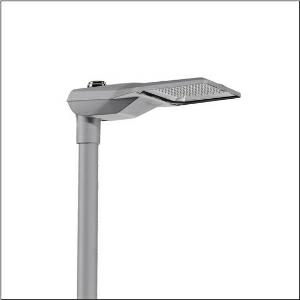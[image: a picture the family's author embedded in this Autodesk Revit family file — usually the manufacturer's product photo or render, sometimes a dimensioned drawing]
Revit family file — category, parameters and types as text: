
# Revit family: streetlight_sl_21_midi___st1_5a_5xe7p37n08mb_d4f4
name_source: partatom
category: Lighting Fixtures
units: mm (PartAtom-declared; Revit-internal decimal feet)

## family parameters
Cut with Voids When Loaded = No
Host = Face
Light Source = No
Part Type = Normal
Room Calculation Point = No
Round Connector Dimension = Use Diameter
Shared = No

## types (1)
- --- (1 x LED, 17960 lm, 136 W, 3000K)
    Apparent Load = 136 VA
    CIE Flux Codes = 22 53 95 100 100
    Color Rendering = 70
    Color Temperature = 3000K
    Default Elevation = 1800 mm
    Description = Streetlight SL 21 midi, mast luminaire, primary light control with lens, of PMMA, primary optical cover: cover, of toughened safety glass, transparent, light distribution: ST1.5a, light emission: direct distribution, primary light characteristic: asymmetric, installation type: side-entry, LED, 3G 2.5mm², High Power LED, rated luminous flux: 17.960lm, luminous efficacy: 132lm/W, light colour: 730, colour temperature: 3000K, control gear: NEMA (7pin), control: overheat protection, pre-setting: linear dimming characteristic, constant luminous flux control, time-dependent luminous flux control, flexible luminous flux parameterisation, mains connection: 220..240V, AC, 50/60Hz, connection cable pre-assembled, cable length: 12,5m, wiring characteristics: H05VV-F, start of lifetime: 136W, end of service life: 142W, reduction: 61W, luminaire housing, of diecast aluminium (EN AC-44300), powder-coated, SITECO metallic grey (DB 702S), corrosivity category C5 high according to DIN EN ISO 12944, multi-level sealing system, sealing non-destructively replaceable, inclination adjustable: 0°, 5°, 10°, 15°, length: 644mm, width: 335mm, height: 110mm, spigot size: 42mm (side-entry), mounting height: 4..8m, protection rating (complete): IP66, insulation class (complete): insulation class I (protective earthing), certification: CE, ENEC, ENEC+, VDE, impact resistance: IK10, permissible operating ambient temperature for outdoor applications: -40..+50°C, standard-compliant lighting for roads and squares, packaging unit: 1 piece

Light Distribution: ST1.5a
    Height = 111 mm
    Lamp = 1 x LED
    Lamp Light Flux = 17960 lm
    Lamp Power = 136 W
    Lamp count = 1
    Length = 644 mm
    Luminous efficacy = 132 lm/W
    Manufacturer = Siteco
    ModVariant = No
    Model = 5XE7P37N08MB
    Number of Poles = 1
    OnlyDefault = Yes
    Power Factor = 1
    Product Name = Streetlight SL 21 midi | ST1.5a
    Product group = mast luminaire | pylon top
    ProductGroupID = 6100
    Protection Class = Protection class I
    Protection Degree = IP 66
    RLX_Detail_Level = 1
    RLX_Emergency_Light_Flux = 0 lm
    RLX_Emergency_Type = 0
    RLX_Emergency_Type_DB = No
    RlxData = <blob elided: 30077 chars, md5=6db74eba>
    Socket = socket
    Standby Power = 0 W
    System Light Flux = 17960 lm
    System Power = 136 W
    Type Comments = factory setting: luminous flux: 100 % | dim-lin: 254 | 695 mA
    Type Image = l_1294377.jpg
    URL = http://relux.com
    VarID = @adj_132957
    Voltage = 0 V
    Weight = 0.00 kg
    Width = 336 mm

## geometry (parser evidence)
native form markers: Blend x4, Sweep x8
no freeform markers — native parametric forms only
